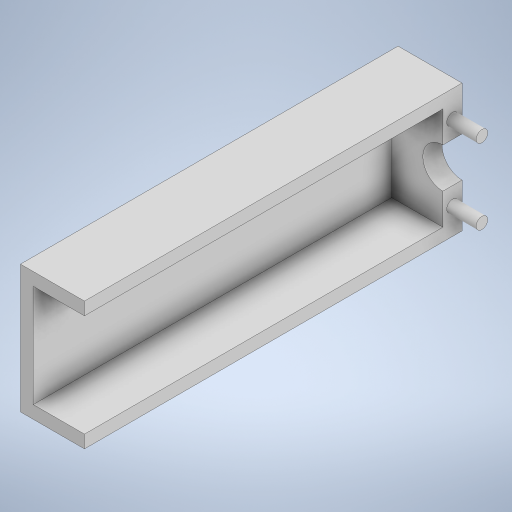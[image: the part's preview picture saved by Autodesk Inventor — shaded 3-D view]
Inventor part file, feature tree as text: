
AUTODESK INVENTOR PART (.ipt)
format: ipt  version: 2023 (Build 270158000, 158)  size: 256,512 bytes
history: native  units: in
note: dims shown in document units (in); Inventor stores cm internally (conversion verified against a paired STEP export)
features: extrude x3, sketch x3, other x1
ambient origin geometry x8: Origin, YZ Plane, XZ Plane, XY Plane, X Axis, Y Axis, Z Axis, Center Point
bodies: Body1 (feature_tree)
feature tree (7):
  other  "솔리드1"
  extrude  "돌출1"  Depth=0.7874in
  extrude  "돌출2"  Depth=1.5748in
  extrude  "돌출4"  Depth=0.4921in
  sketch  "스케치1"
  sketch  "스케치2"
  sketch  "스케치4"
